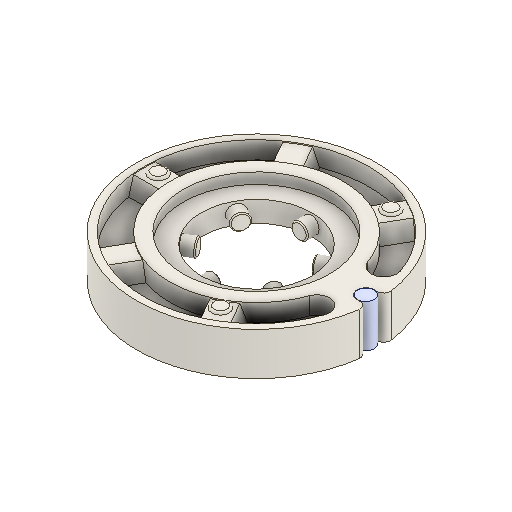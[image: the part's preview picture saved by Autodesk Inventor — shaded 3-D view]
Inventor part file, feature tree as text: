
AUTODESK INVENTOR PART (.ipt)
format: ipt  version: 2022 (Build 260153000, 153)  size: 294,400 bytes
history: native  units: mm
features: other x1, mirror x1
ambient origin geometry x8: Origin, YZ Plane, XZ Plane, XY Plane, X Axis, Y Axis, Z Axis, Center Point
bodies: Volumenkörper1 (feature_tree), Volumenkörper2 (feature_tree)
feature tree (2):
  other  "Boss-Extrude4"
  mirror  "Mirror1"
